# Revit family: KCA - Componente
name_source: partatom
category: Generic Models
units: mm (PartAtom-declared; Revit-internal decimal feet)

## family parameters
Always vertical = Yes
Can host rebar = No
Cut with Voids When Loaded = No
Maintain Annotation Orientation = No
Part Type = Normal
Room Calculation Point = No
Round Connector Dimension = Use Diameter
Shared = No
Work Plane-Based = No

## types (9) — shared parameters
P = 1000 mm  [stored 3.28084 ft]
zero-valued in all types: Default Elevation

## per-type parameters (varying)
| type | H | L |
| 1 x 1 x 6 | 6000 mm  [stored 19.685 ft] | 1000 mm  [stored 3.28084 ft] |
| 1 x 2.5 x 5.5 | 5500 mm  [stored 18.0446 ft] | 2500 mm  [stored 8.2021 ft] |
| 1 x 4 x 5 | 5000 mm  [stored 16.4042 ft] | 4000 mm  [stored 13.1234 ft] |
| 1 x 2.5 x 6.5 | 6500 mm  [stored 21.3255 ft] | 2500 mm  [stored 8.2021 ft] |
| 1 x 1 x 8 | 8000 mm  [stored 26.2467 ft] | 1000 mm  [stored 3.28084 ft] |
| 1 x 4 x 7 | 7000 mm  [stored 22.9659 ft] | 4000 mm  [stored 13.1234 ft] |
| 1 x 1 x 4.5 | 4500 mm | 1000 mm  [stored 3.28084 ft] |
| 1 x 2.5 x 7.5 | 7500 mm  [stored 24.6063 ft] | 2500 mm  [stored 8.2021 ft] |
| 1 x 2.5 x 4 | 4000 mm  [stored 13.1234 ft] | 2500 mm  [stored 8.2021 ft] |

note: [stored X ft] marks values corroborated as IEEE doubles in the binary element streams (Revit-internal decimal feet)

## geometry (parser evidence)
native form markers: Sweep x3
no freeform markers — native parametric forms only
